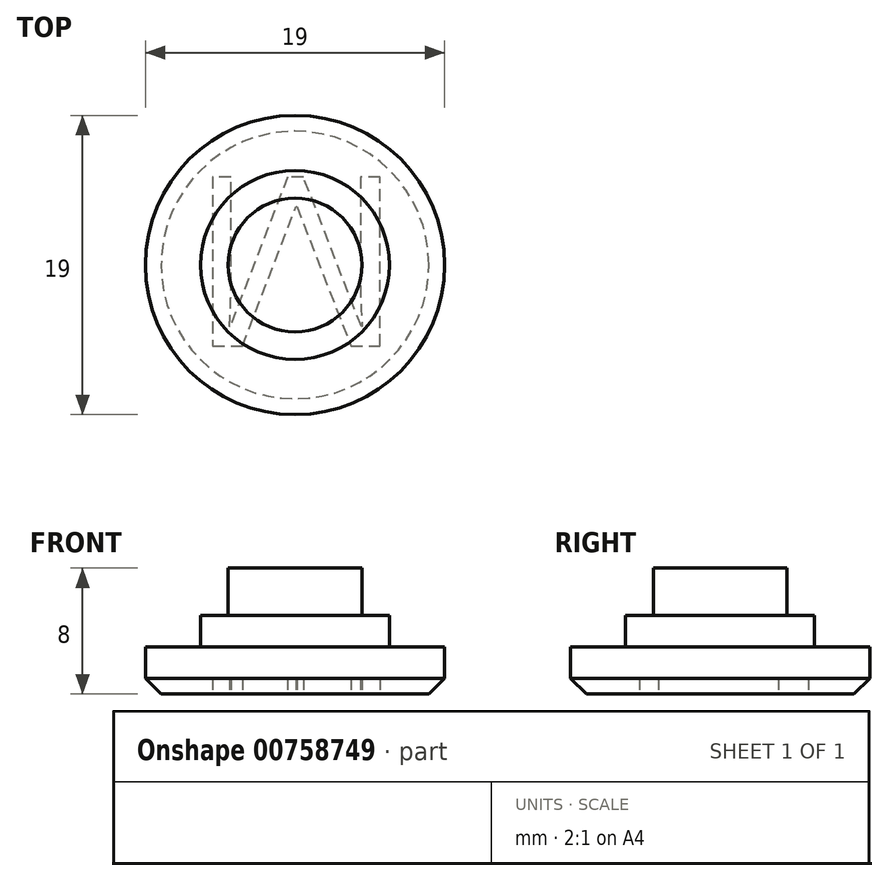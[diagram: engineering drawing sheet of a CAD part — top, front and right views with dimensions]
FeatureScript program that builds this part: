
annotation { "Feature Type Name" : "Feature", "Feature Type Description" : "" }
export const myFeature = defineFeature(function(context is Context, id is Id, definition is map)
    precondition{}
    {
        {
            assignVariable(context, id + "F0", {"name" : "clearance", "anyValue" : 2});
        }
        {
            assignVariable(context, id + "F1", {"name" : "capthick", "anyValue" : 3});
        }
        {
            var Q0;
            Q0=qCreatedBy(makeId("Top.planeOp"),FACE);
            var sketch = newSketch(context, id + "F2", { "sketchPlane" : qUnion([Q0])});
            skCircle(sketch, "E0", {"center": v(0, 0) * mm, "radius": 4.25 * mm});
            skCircle(sketch, "E1", {"center": v(0, 0) * mm, "radius": 6 * mm});
            skCircle(sketch, "E2", {"center": v(0, 0) * mm, "radius": 9.5 * mm});
            skSolve(sketch);
        }
        {
            var Q0;
            Q0=makeQuery(id+"F2.imprint","IMPRINT",FACE,{"disambiguationData":[TD([[makeQuery(id+"F2.imprint","IMPRINT",EDGE,{"derivedFrom":sQuery(id+"F2.wireOp",EDGE,"E1")}),-1.0]])]});
            extrude(context, id + "F3", {"entities" : qUnion([Q0]), "depth" : (getVariable(context, 'capthick')) * mm, "offsetDistance" : 25 * mm});
        }
        {
            var Q0;
            Q0=makeQuery(id+"F2.imprint","IMPRINT",FACE,{"disambiguationData":[TD([[makeQuery(id+"F2.imprint","IMPRINT",EDGE,{"derivedFrom":sQuery(id+"F2.wireOp",EDGE,"E0")}),-1.0]])]});
            extrude(context, id + "F4", {"entities" : qUnion([Q0]), "operationType" : NewBodyOperationType.ADD, "depth" : (getVariable(context, 'clearance') + getVariable(context, 'capthick')) * mm, "offsetDistance" : 25 * mm});
        }
        {
            var Q0;
            Q0=makeQuery(id+"F2.imprint","IMPRINT",FACE,{"disambiguationData":[TD([[makeQuery(id+"F2.imprint","IMPRINT",EDGE,{"derivedFrom":sQuery(id+"F2.wireOp",EDGE,"E0")}),1.0]])]});
            extrude(context, id + "F5", {"entities" : qUnion([Q0]), "operationType" : NewBodyOperationType.ADD, "depth" : (getVariable(context, 'clearance') + getVariable(context, 'capthick') + 3) * mm, "offsetDistance" : 25 * mm});
        }
        {
            var Q0;
            Q0=makeQuery(id+"F3.opExtrude","CAP_EDGE",EDGE,{"disambiguationData":[OSD([sQuery(id+"F2.wireOp",EDGE,"E2")])],"isStart":true});
            chamfer(context, id + "F6", {"entities" : qUnion([Q0]), "width" : 1 * mm, "tangentPropagation" : true});
        }
        {
            var Q0;
            {var subQ0=sQuery(id+"F2.wireOp",EDGE,"E0");var subQ1=sQuery(id+"F2.wireOp",EDGE,"E1");Q0=makeQuery(id+"F5.boolean.opBoolean","MERGE",FACE,{"derivedFrom":[makeQuery(id+"F4.boolean.opBoolean","MERGE",FACE,{"derivedFrom":[makeQuery(id+"F3.opExtrude","CAP_FACE",FACE,{"disambiguationData":[OSD([subQ1,sQuery(id+"F2.wireOp",EDGE,"E2")])],"isStart":true}),makeQuery(id+"F4.opExtrude","CAP_FACE",FACE,{"disambiguationData":[OSD([subQ0,subQ1])],"isStart":true})]}),makeQuery(id+"F5.opExtrude","CAP_FACE",FACE,{"disambiguationData":[OSD([subQ0])],"isStart":true})]});}
            var sketch = newSketch(context, id + "F7", { "sketchPlane" : qUnion([Q0])});
            skText(sketch, "E3", { "text": "M", "fontName": "OpenSans-Regular.ttf"});
            const initialGuessF7  = {"E3": [-0.0067, -0.0056, 1, 0, 0.01083]};
            skSetInitialGuess(sketch, initialGuessF7);
            skSolve(sketch);
        }
        {
            var Q0;
            Q0=makeQuery(id+"F7.imprint","IMPRINT",FACE,{"disambiguationData":[TD([[makeQuery(id+"F7.imprint","IMPRINT",EDGE,{"derivedFrom":sQuery(id+"F7.wireOp",EDGE,"E3.sketch_text.stroke-0")}),-1.0]])]});
            extrude(context, id + "F8", {"entities" : qUnion([Q0]), "operationType" : NewBodyOperationType.REMOVE, "oppositeDirection" : true, "depth" : 1 * mm, "offsetDistance" : 25 * mm});
        }
    });
